# Revit family: Банкетка для раздевалок «Бавария» Арт 20546
name_source: partatom
category: Антураж
revit_build: Autodesk Revit 2018 (Build: 20180423_1000(x64)
units: mm (PartAtom-declared; Revit-internal decimal feet)

## family parameters
Всегда вертикально = Да
Источник визуального образа = Геометрия семейства
На основе рабочей плоскости = Нет
Общий = Нет
При загрузке вырезать с полостями = Нет
Точка расчета площади = Нет

## types (3) — shared parameters
URL = https://hobbyka.ru
Артикул товара = Арт. 20546
Высота = 460 мм
Группа модели = Скамейки для раздевалок
Изготовитель = ООО «Хоббика»
Изображение типоразмера = Банкетка для раздевалок «Бавария» Арт 20546.jpg
Материал изделия = Сталь, кожзаменитель
Ширина = 400 мм

## per-type parameters (varying)
| type | Версия 1,2 м | Версия 1,5 м | Версия 2,0 м | Длина | Описание |
| Версия 1,2 м | Да | Нет | Нет | 1200 мм | Банкетка для раздевалок «Бавария». Версия 1,2 м |
| Версия 1,5 м | Нет | Да | Нет | 1500 мм | Банкетка для раздевалок «Бавария». Версия 1,5 м |
| Версия 2,0 м | Нет | Нет | Да | 2000 мм | Банкетка для раздевалок «Бавария». Версия 2,0 м |
